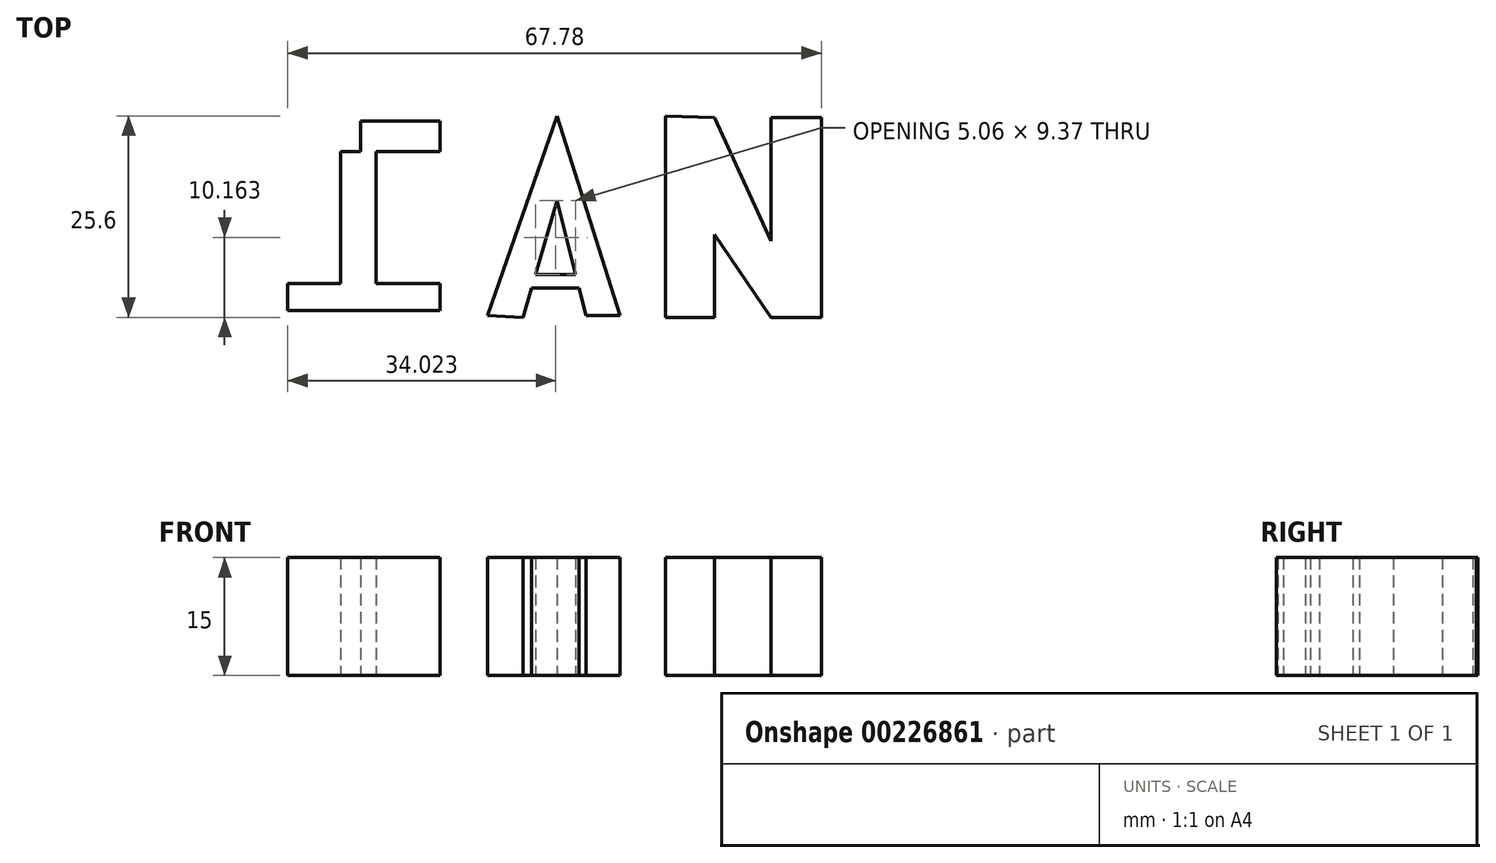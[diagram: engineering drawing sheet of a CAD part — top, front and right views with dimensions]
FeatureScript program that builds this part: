
annotation { "Feature Type Name" : "Feature", "Feature Type Description" : "" }
export const myFeature = defineFeature(function(context is Context, id is Id, definition is map)
    precondition{}
    {
        {
            var Q0;
            Q0=qCreatedBy(makeId("Top.planeOp"),FACE);
            var sketch = newSketch(context, id + "F0", { "sketchPlane" : qUnion([Q0])});
            skLineSegment(sketch, "E0", {"start": v(-44.97, 37.87) * mm, "end": v(-44.97, 13.77) * mm});
            skLineSegment(sketch, "E1", {"start": v(-54.22, 13.77) * mm, "end": v(-34.86, 13.77) * mm});
            skLineSegment(sketch, "E2", {"start": v(-44.97, 37.87) * mm, "end": v(-55.08, 37.87) * mm});
            skLineSegment(sketch, "E3", {"start": v(-55.08, 37.87) * mm, "end": v(-34.86, 37.87) * mm});
            skPoint(sketch, "E3.endSnap0", {"position": v(-50.03, 37.87) * mm});
            skLineSegment(sketch, "E4", {"start": v(-50.03, 37.87) * mm, "end": v(-44.97, 37.87) * mm});
            skPoint(sketch, "E5.endSnap0", {"position": v(-47.5, 37.87) * mm});
            skLineSegment(sketch, "E6", {"start": v(-34.86, 37.87) * mm, "end": v(-34.86, 34) * mm});
            skLineSegment(sketch, "E7", {"start": v(-34.86, 34) * mm, "end": v(-55.3, 34) * mm});
            skLineSegment(sketch, "E8", {"start": v(-55.3, 34) * mm, "end": v(-55.08, 37.87) * mm});
            skLineSegment(sketch, "E9", {"start": v(-54.22, 13.77) * mm, "end": v(-54.22, 17.21) * mm});
            skLineSegment(sketch, "E10", {"start": v(-54.22, 17.21) * mm, "end": v(-34.86, 17.21) * mm});
            skLineSegment(sketch, "E11", {"start": v(-34.86, 17.21) * mm, "end": v(-34.86, 13.77) * mm});
            skLineSegment(sketch, "E12", {"start": v(-43.03, 34) * mm, "end": v(-43.03, 17.21) * mm});
            skLineSegment(sketch, "E13", {"start": v(-47.5, 34) * mm, "end": v(-47.5, 17.21) * mm});
            skLineSegment(sketch, "E14", {"start": v(-24.31, 12.9) * mm, "end": v(-20.01, 27.76) * mm});
            skLineSegment(sketch, "E15", {"start": v(-20.01, 27.76) * mm, "end": v(-16.35, 13.13) * mm});
            skLineSegment(sketch, "E16", {"start": v(-16.35, 13.13) * mm, "end": v(-12.05, 13.13) * mm});
            skLineSegment(sketch, "E17", {"start": v(-12.05, 13.13) * mm, "end": v(-20.01, 38.51) * mm});
            skLineSegment(sketch, "E18", {"start": v(-20.01, 38.51) * mm, "end": v(-28.83, 13.13) * mm});
            skLineSegment(sketch, "E19", {"start": v(-28.83, 13.13) * mm, "end": v(-24.31, 12.9) * mm});
            skLineSegment(sketch, "E20", {"start": v(-17.67, 18.4) * mm, "end": v(-22.73, 18.4) * mm});
            skLineSegment(sketch, "E21", {"start": v(-17.23, 16.62) * mm, "end": v(-23.24, 16.62) * mm});
            skLineSegment(sketch, "E22", {"start": v(0, 12.9) * mm, "end": v(0, 23.45) * mm});
            skLineSegment(sketch, "E23", {"start": v(0, 23.45) * mm, "end": v(7.17, 12.9) * mm});
            skLineSegment(sketch, "E24", {"start": v(7.17, 38.3) * mm, "end": v(13.56, 38.3) * mm});
            skLineSegment(sketch, "E25", {"start": v(13.56, 38.3) * mm, "end": v(13.56, 12.9) * mm});
            skLineSegment(sketch, "E26", {"start": v(7.17, 12.9) * mm, "end": v(13.56, 12.9) * mm});
            skLineSegment(sketch, "E27", {"start": v(7.17, 38.3) * mm, "end": v(7.17, 22.6) * mm});
            skLineSegment(sketch, "E28", {"start": v(0, 12.9) * mm, "end": v(-6.24, 12.9) * mm});
            skLineSegment(sketch, "E29", {"start": v(-6.24, 12.9) * mm, "end": v(-6.24, 38.51) * mm});
            skLineSegment(sketch, "E30", {"start": v(7.17, 22.6) * mm, "end": v(0, 38.3) * mm});
            skLineSegment(sketch, "E31", {"start": v(0, 38.3) * mm, "end": v(-6.24, 38.51) * mm});
            skSolve(sketch);
        }
        {
            var Q0;
            {var subQ4=sQuery(id+"F0.wireOp",EDGE,"E4");Q0=makeQuery(id+"F0.imprint","IMPRINT",FACE,{"disambiguationData":[TD([[makeQuery(id+"F0.imprint","IMPRINT",EDGE,{"derivedFrom":subQ4}),-1.0]])]});}
            var Q1;
            {var subQ1=sQuery(id+"F0.wireOp",EDGE,"E6");Q1=makeQuery(id+"F0.imprint","IMPRINT",FACE,{"disambiguationData":[TD([[makeQuery(id+"F0.imprint","IMPRINT",EDGE,{"derivedFrom":subQ1}),-1.0]])]});}
            var Q2;
            {var subQ1=sQuery(id+"F0.wireOp",EDGE,"E9");Q2=makeQuery(id+"F0.imprint","IMPRINT",FACE,{"disambiguationData":[TD([[makeQuery(id+"F0.imprint","IMPRINT",EDGE,{"derivedFrom":subQ1}),-1.0]])]});}
            var Q3;
            {var subQ3=sQuery(id+"F0.wireOp",EDGE,"E11");Q3=makeQuery(id+"F0.imprint","IMPRINT",FACE,{"disambiguationData":[TD([[makeQuery(id+"F0.imprint","IMPRINT",EDGE,{"derivedFrom":subQ3}),-1.0]])]});}
            var Q4;
            {var subQ10=sQuery(id+"F0.wireOp",EDGE,"E16");Q4=makeQuery(id+"F0.imprint","IMPRINT",FACE,{"disambiguationData":[TD([[makeQuery(id+"F0.imprint","IMPRINT",EDGE,{"derivedFrom":subQ10}),1.0]])]});}
            var Q5;
            {var subQ0=sQuery(id+"F0.wireOp",EDGE,"E20");Q5=makeQuery(id+"F0.imprint","IMPRINT",FACE,{"disambiguationData":[TD([[makeQuery(id+"F0.imprint","IMPRINT",EDGE,{"derivedFrom":subQ0}),1.0]])]});}
            var Q6;
            {var subQ5=sQuery(id+"F0.wireOp",EDGE,"E12");Q6=makeQuery(id+"F0.imprint","IMPRINT",FACE,{"disambiguationData":[TD([[makeQuery(id+"F0.imprint","IMPRINT",EDGE,{"derivedFrom":subQ5}),-1.0]])]});}
            var Q7;
            {var subQ5=sQuery(id+"F0.wireOp",EDGE,"E13");Q7=makeQuery(id+"F0.imprint","IMPRINT",FACE,{"disambiguationData":[TD([[makeQuery(id+"F0.imprint","IMPRINT",EDGE,{"derivedFrom":subQ5}),1.0]])]});}
            var Q8;
            Q8=makeQuery(id+"F0.imprint","IMPRINT",FACE,{"disambiguationData":[TD([[makeQuery(id+"F0.imprint","IMPRINT",EDGE,{"derivedFrom":sQuery(id+"F0.wireOp",EDGE,"E22")}),1.0]])]});
            extrude(context, id + "F1", {"entities" : qUnion([Q0, Q1, Q2, Q3, Q4, Q5, Q6, Q7, Q8]), "depth" : 15 * mm});
        }
    });
